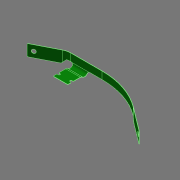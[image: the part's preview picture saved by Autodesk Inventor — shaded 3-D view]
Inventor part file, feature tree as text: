
AUTODESK INVENTOR PART (.ipt)
format: ipt  version: 2020.2 (Build 242310000, 310)  size: 359,936 bytes
history: native  units: in
note: dims shown in document units (in); Inventor stores cm internally (conversion verified against a paired STEP export)
features: sheet_metal_op x4, fillet x2, sketch x1, extrude x1
ambient origin geometry x8: Origin, YZ Plane, XZ Plane, XY Plane, X Axis, Y Axis, Z Axis, Center Point
bodies: Solid7 (feature_tree), Solid27 (feature_tree)
feature tree (8):
  sketch  "Sketch2-<F>"  dims[d33=0.063in d34=0.0315in d35=0.0158in d36=1.257in d37=0.0985in d38=0.2575in d40=0.372in d41=135.0deg d42=0.2205in d43=135.0deg d44=0.228in d45=0.0432in d46=0.0432in d47=0.0158in d48=0.0315in d49=0.063in d50=0.063in d54=0.083in d55=0.1885in d57=0.1085in d58=0.0335in d59=0.043in d60=0.0335in d61=0.043in d62=0.0024in d63=0.0in d67=0.006in d68=0.02in d69=0.0024in d70=0.0024in d71=0.0012in d72=0.0048in d73=0.0024in d74=0.1855in d75=0.125in d76=0.0024in d77=0.0012in d78=0.0048in d79=0.0024in d80=0.2542in d81=0.675in d83=0.0024in d84=0.0012in d85=0.0048in d86=0.0024in d87=0.8933in d88=0.026in d89=0.1305in d90=0.0024in d91=0.0012in d92=0.0048in d93=0.0024in d94=0.2749in d95=0.0265in d96=0.0633in]
  extrude  "Extrusion1"  Depth=0.0265in
  fillet  "Fillet1"  Radius=0.0158in
  fillet  "Fillet2"  Radius=1.257in
  sheet_metal_op  "Fold1"
  sheet_metal_op  "Fold2"
  sheet_metal_op  "Fold3"
  sheet_metal_op  "Fold4"
